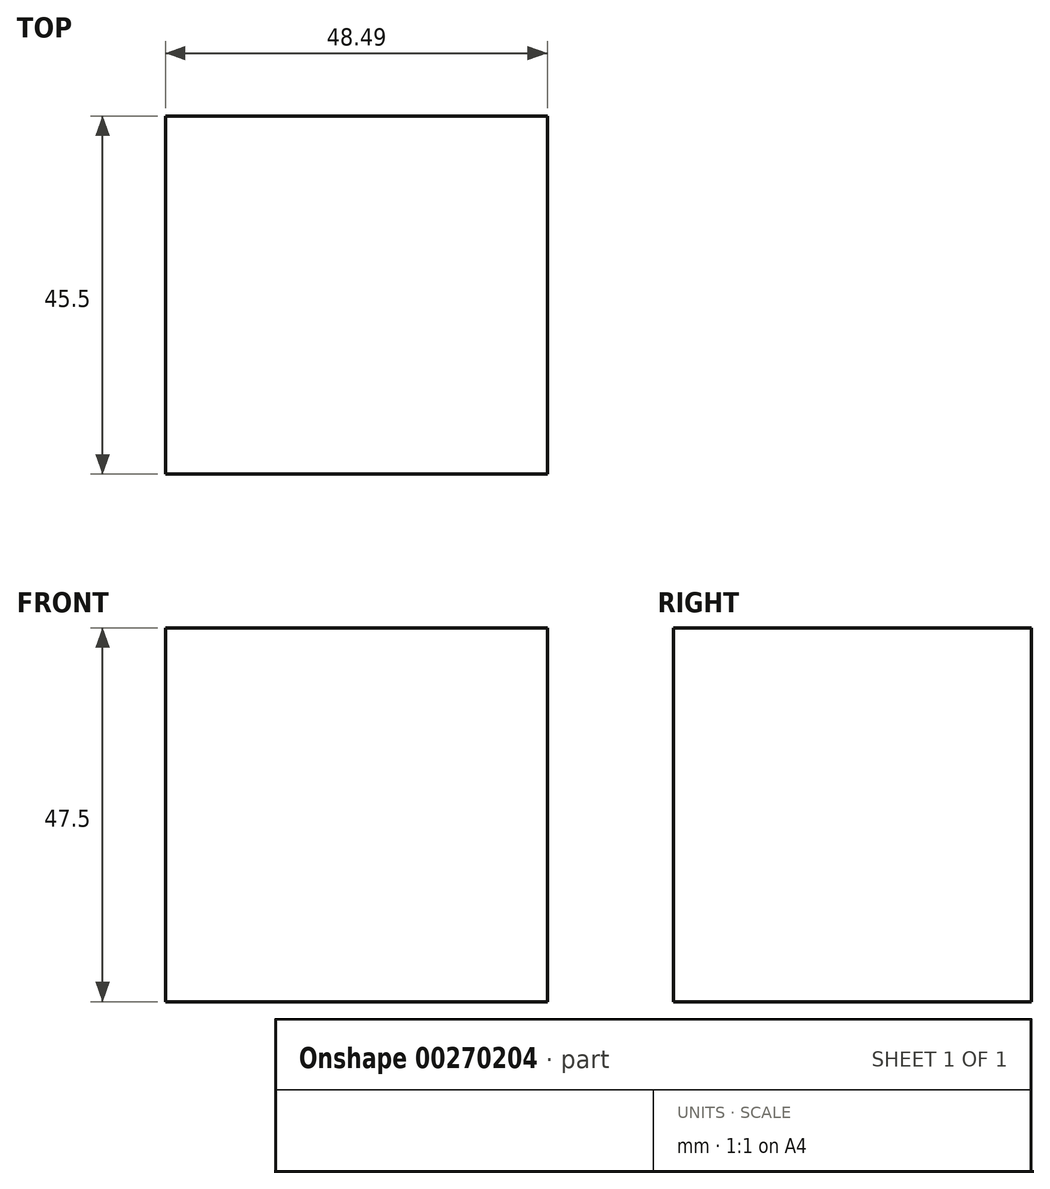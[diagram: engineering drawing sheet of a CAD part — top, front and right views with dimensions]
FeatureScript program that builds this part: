
annotation { "Feature Type Name" : "Feature", "Feature Type Description" : "" }
export const myFeature = defineFeature(function(context is Context, id is Id, definition is map)
    precondition{}
    {
        {
            var Q0;
            Q0=qCreatedBy(makeId("Top.planeOp"),FACE);
            var sketch = newSketch(context, id + "F0", { "sketchPlane" : qUnion([Q0])});
            skLineSegment(sketch, "E0.bottom", {"start": v(-48.5, 0) * mm, "end": v(0, 0) * mm});
            skLineSegment(sketch, "E0.top", {"start": v(-48.5, -45.5) * mm, "end": v(0, -45.5) * mm});
            skLineSegment(sketch, "E0.left", {"start": v(-48.5, 0) * mm, "end": v(-48.5, -45.5) * mm});
            skLineSegment(sketch, "E0.right", {"start": v(0, 0) * mm, "end": v(0, -45.5) * mm});
            skLineSegment(sketch, "E1.bottom", {"start": v(-43.54, 13.43) * mm, "end": v(-27.77, 13.43) * mm});
            skLineSegment(sketch, "E1.top", {"start": v(-43.54, 21.38) * mm, "end": v(-27.77, 21.38) * mm});
            skLineSegment(sketch, "E1.left", {"start": v(-27.77, 21.38) * mm, "end": v(-27.77, 13.43) * mm});
            skLineSegment(sketch, "E1.right", {"start": v(-43.54, 21.38) * mm, "end": v(-43.54, 13.43) * mm});
            skSolve(sketch);
        }
        {
            var Q0;
            Q0=makeQuery(id+"F0.imprint","IMPRINT",FACE,{"disambiguationData":[TD([[makeQuery(id+"F0.imprint","IMPRINT",EDGE,{"derivedFrom":sQuery(id+"F0.wireOp",EDGE,"E0.bottom")}),-1.0]])]});
            extrude(context, id + "F1", {"entities" : qUnion([Q0]), "depth" : 47.5 * mm});
        }
    });
